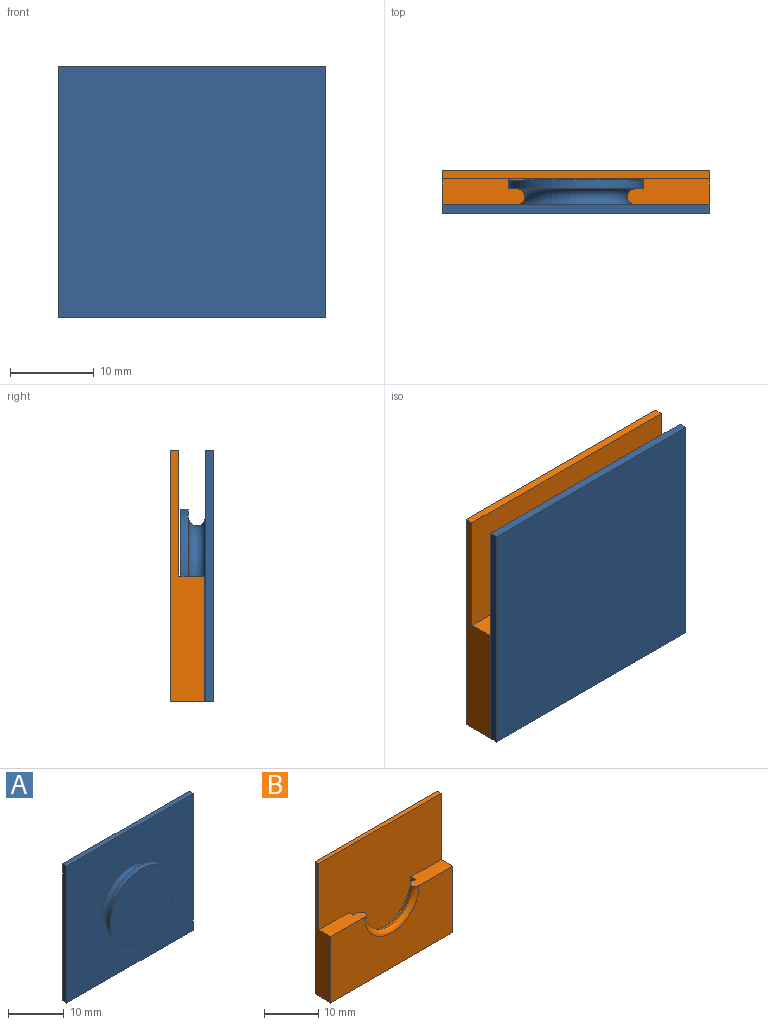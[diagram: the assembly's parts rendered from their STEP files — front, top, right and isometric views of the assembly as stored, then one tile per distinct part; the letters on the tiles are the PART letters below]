
ASSEMBLY  parts=2 mates=1
PART A: 10 faces, bbox 32x4x30 mm
  f0: plane 32x1mm, normal (0,0,-1), area 32mm2, adj f1,f3,f4,f5
  f1: plane 30x1mm, normal (1,0,0), area 30mm2, adj f0,f2,f4,f5
  f2: plane 32x1mm, normal (0,0,1), area 32mm2, adj f1,f3,f4,f5
  f3: plane 30x1mm, normal (-1,0,0), area 30mm2, adj f0,f2,f4,f5
  f4: plane 32x30mm, normal (0,-1,0), area 806.1mm2, adj f0,f1,f2,f3,f9
  f5: plane 32x30mm, normal (0,1,0), area 960mm2, adj f0,f1,f2,f3
  f6: cylinder r=8mm len=16mm, axis (0,-1,0), area 50.3mm2, adj f7,f8
  f7: plane 16x16mm, normal (0,-1,0), area 201.1mm2, adj f6
  f8: plane 16x16mm, normal (0,1,0), area 47.1mm2, adj f6,f9
  f9: torus R=7mm, axis (0,-1,0), area 125.6mm2, adj f4,f8
PART B: 13 faces, bbox 32x4.1x30 mm
  f0: plane 32x23.1mm, normal (0,-1,0), area 583.1mm2, adj f2,f3,f4,f6,f7,f8
  f1: plane 32x4.1mm, normal (0,0,-1), area 131.2mm2, adj f2,f4,f5,f10
  f2: plane 30x4.1mm, normal (1,0,0), area 76.5mm2, adj f0,f1,f3,f5,f7,f10
  f3: plane 32x1mm, normal (0,0,1), area 32mm2, adj f0,f2,f4,f5
  f4: plane 30x4.1mm, normal (-1,0,0), area 76.5mm2, adj f0,f1,f3,f5,f6,f10
  f5: plane 32x30mm, normal (0,1,0), area 960mm2, adj f1,f2,f3,f4
  f6: plane 9.9x3.1mm, normal (0,0,1), area 27.9mm2, adj f0,f4,f8,f9,f10,f11,f12
  f7: plane 9.9x3.1mm, normal (0,0,1), area 27.9mm2, adj f0,f2,f8,f9,f10,f11,f12
  f8: cylinder r=8.1mm len=16.2mm, axis (0,-1,0), area 30.5mm2, adj f0,f6,f7,f9
  f9: plane 16.2x8.1mm, normal (0,1,0), area 23.9mm2, adj f6,f7,f8,f12
  f10: plane 32x15mm, normal (0,-1,0), area 400.8mm2, adj f1,f2,f4,f6,f7,f11
  f11: torus R=7.1mm, axis (0,-1,0), area 30.9mm2, adj f6,f7,f10,f12
  f12: torus R=7.1mm, axis (0,-1,0), area 30.9mm2, adj f6,f7,f9,f11
PLACE A rot(axis=(1,0,0),180deg) t=(0,-5.15,0)mm
PLACE B at identity
MATE fastened A.f9 <-> B.f11  axis (0,1,0) through (0,-3.15,0)mm
